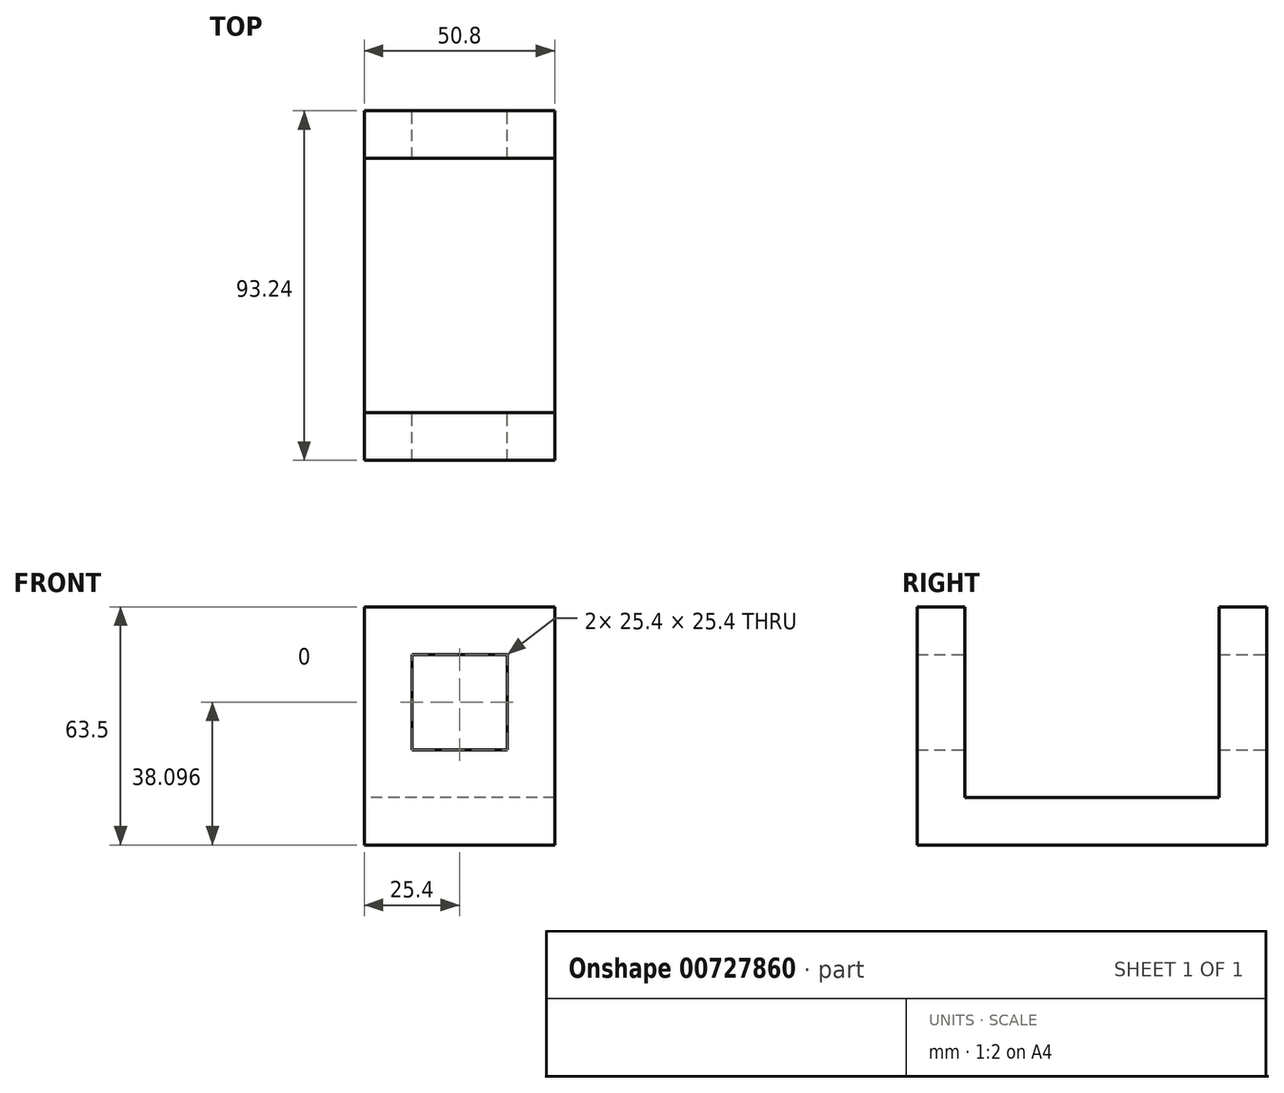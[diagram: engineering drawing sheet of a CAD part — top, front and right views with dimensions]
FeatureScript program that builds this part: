
annotation { "Feature Type Name" : "Feature", "Feature Type Description" : "" }
export const myFeature = defineFeature(function(context is Context, id is Id, definition is map)
    precondition{}
    {
        {
            var Q0;
            Q0=qCreatedBy(makeId("Right.planeOp"),FACE);
            var sketch = newSketch(context, id + "F0", { "sketchPlane" : qUnion([Q0])});
            skLineSegment(sketch, "E0", {"start": v(-46.15, 35.9) * mm, "end": v(-46.15, -27.6) * mm});
            skLineSegment(sketch, "E1", {"start": v(47.09, 35.9) * mm, "end": v(47.09, -27.6) * mm});
            skLineSegment(sketch, "E2", {"start": v(34.39, 35.9) * mm, "end": v(47.09, 35.9) * mm});
            skLineSegment(sketch, "E3", {"start": v(-46.15, 35.9) * mm, "end": v(-33.45, 35.9) * mm});
            skLineSegment(sketch, "E4", {"start": v(-33.45, -14.9) * mm, "end": v(-33.45, 35.9) * mm});
            skLineSegment(sketch, "E5", {"start": v(34.39, 35.9) * mm, "end": v(34.39, -14.9) * mm});
            skLineSegment(sketch, "E6", {"start": v(-33.45, -14.9) * mm, "end": v(34.39, -14.9) * mm});
            skLineSegment(sketch, "E7", {"start": v(-46.15, -27.6) * mm, "end": v(47.09, -27.6) * mm});
            skSolve(sketch);
        }
        {
            var Q0;
            Q0=makeQuery(id+"F0.imprint","IMPRINT",FACE,{"disambiguationData":[TD([[makeQuery(id+"F0.imprint","IMPRINT",EDGE,{"derivedFrom":sQuery(id+"F0.wireOp",EDGE,"E0")}),1.0]])]});
            extrude(context, id + "F1", {"entities" : qUnion([Q0]), "depth" : 50.8 * mm, "offsetDistance" : 25.4 * mm});
        }
        {
            var Q0;
            Q0=makeQuery(id+"F1.opExtrude","SWEPT_FACE",FACE,{"disambiguationData":[OSD([sQuery(id+"F0.wireOp",EDGE,"E1")])]});
            var sketch = newSketch(context, id + "F2", { "sketchPlane" : qUnion([Q0])});
            skPoint(sketch, "E8.middle", {"position": v(-18.34, 0) * mm});
            skLineSegment(sketch, "E9.left", {"start": v(-29.04, -23.2) * mm, "end": v(-29.04, -23.2) * mm});
            skLineSegment(sketch, "E9.right", {"start": v(-18.94, -23.2) * mm, "end": v(-18.94, -23.2) * mm});
            skPoint(sketch, "E9.middle", {"position": v(-23.99, -23.2) * mm});
            skPoint(sketch, "E8.right.start.orphan", {"position": v(-12.7, 23.2) * mm});
            skPoint(sketch, "E8.left.start.orphan", {"position": v(-23.99, 23.2) * mm});
            skPoint(sketch, "E10.orphan", {"position": v(-12.7, -23.2) * mm});
            skLineSegment(sketch, "E11.bottom", {"start": v(-12.7, 23.2) * mm, "end": v(-38.1, 23.2) * mm});
            skLineSegment(sketch, "E11.top", {"start": v(-12.7, -2.2) * mm, "end": v(-38.1, -2.2) * mm});
            skLineSegment(sketch, "E11.left", {"start": v(-12.7, 23.2) * mm, "end": v(-12.7, -2.2) * mm});
            skLineSegment(sketch, "E11.right", {"start": v(-38.1, 23.2) * mm, "end": v(-38.1, -2.2) * mm});
            skPoint(sketch, "E11.middle", {"position": v(-25.4, 10.5) * mm});
            skSolve(sketch);
        }
        {
            var Q0;
            Q0=makeQuery(id+"F2.imprint","IMPRINT",FACE,{"disambiguationData":[TD([[makeQuery(id+"F2.imprint","IMPRINT",EDGE,{"derivedFrom":sQuery(id+"F2.wireOp",EDGE,"E8.bottom")}),-1.0]])]});
            var sketch = newSketch(context, id + "F3", { "sketchPlane" : qUnion([Q0])});
            skSolve(sketch);
        }
        {
            var Q0;
            Q0 = qSketchRegion(id + "F3", true);
            var Q1;
            Q1=makeQuery(id+"F2.imprint","IMPRINT",FACE,{"disambiguationData":[TD([[makeQuery(id+"F2.imprint","IMPRINT",EDGE,{"derivedFrom":sQuery(id+"F2.wireOp",EDGE,"E11.bottom")}),1.0]])]});
            extrude(context, id + "F4", {"entities" : qUnion([Q0, Q1]), "operationType" : NewBodyOperationType.REMOVE, "oppositeDirection" : true, "depth" : 128.02 * mm, "offsetDistance" : 25.4 * mm});
        }
    });
